# Revit family: Astro _ SKYE Spike Spot
name_source: partatom
category: Lighting Fixtures
revit_build: Autodesk Revit 2018 (Build: 20170223_1515(x64)
units: mm (PartAtom-declared; Revit-internal decimal feet)

## family parameters
Always vertical = Yes
Cut with Voids When Loaded = No
Light Source = Yes
OmniClass Number = 23.80.70.00
OmniClass Title = Lighting
Part Type = Normal
Room Calculation Point = No
Round Connector Dimension = Use Diameter
Shared = No
Work Plane-Based = No

## types (1)
- AstroAstro Skye Spike Spot
    Color Filter = 16777215
    Dimmable = Yes - Driver Dependent
    Dimming Lamp Color Temperature Shift = <None>
    Dimming Method = Driver Dependent
    Dims MM = 330 x 80 x 100
    Driver Included = No
    Driver Required = yes
    Efficacy (lm/W) = 68
    Electrical Class = 3
    Emit from Line Length = 610 mm
    Lamp = LED
    Length of Cable Supplied = 1300
    Location Rating = IP65
    Main Finish = Brushed Stainless Steel
    Main Material = Stainless Steel
    Photometric Web File = 1386001_Skye Spike Spot_Photometry_IES_Iss. 01.ies
    Power (W) = 9.7 W ( inc driver )
    Product Location = Ground, Zone 1,2,3
    Product Name = Skye Spike Spot
    Product SKU = 1386001
    Product URL = https://www.astrolighting.com
    Tilt Angle = 60.00°
    Weight KG = 0.94

## geometry (parser evidence)
native form markers: Sweep x3
no freeform markers — native parametric forms only
